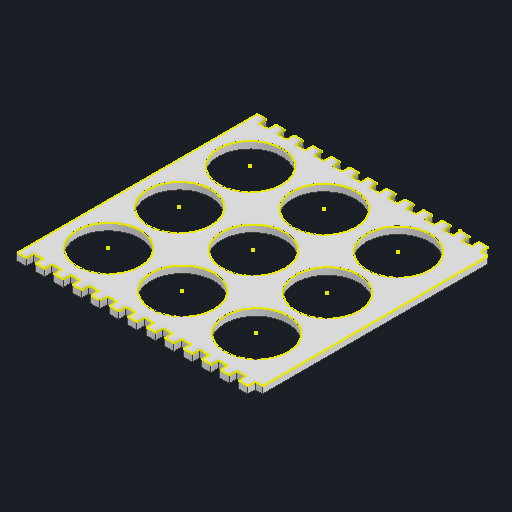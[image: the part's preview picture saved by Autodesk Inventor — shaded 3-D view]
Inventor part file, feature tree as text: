
AUTODESK INVENTOR PART (.ipt)
format: ipt  version: 2023 (Build 270158030, 158C)  size: 466,944 bytes
history: native  units: mm
features: sketch x3, extrude x2, mirror x1, projected_geometry x1
ambient origin geometry x8: Origin, YZ Plane, XZ Plane, XY Plane, X Axis, Y Axis, Z Axis, Center Point
bodies: Solid1 (feature_tree)
feature tree (7):
  extrude  "Extrusion1"  Depth=4.0mm TaperAngle=0.0deg
  mirror  "Mirror1"
  extrude  "Extrusion2"  Depth=6.5mm TaperAngle=0.0deg
  sketch  "Sketch3"
  sketch  "Sketch1"  dims[d0=180.0deg d1=4.0mm d2=0.0mm]
  sketch  "Sketch2"  dims[d3=132.004478mm d5=0.0mm d6=3.880396mm d7=47.003386mm d11=8.0mm d12=6.5mm d13=0.0mm]
  projected_geometry  "Projected Loop1"
